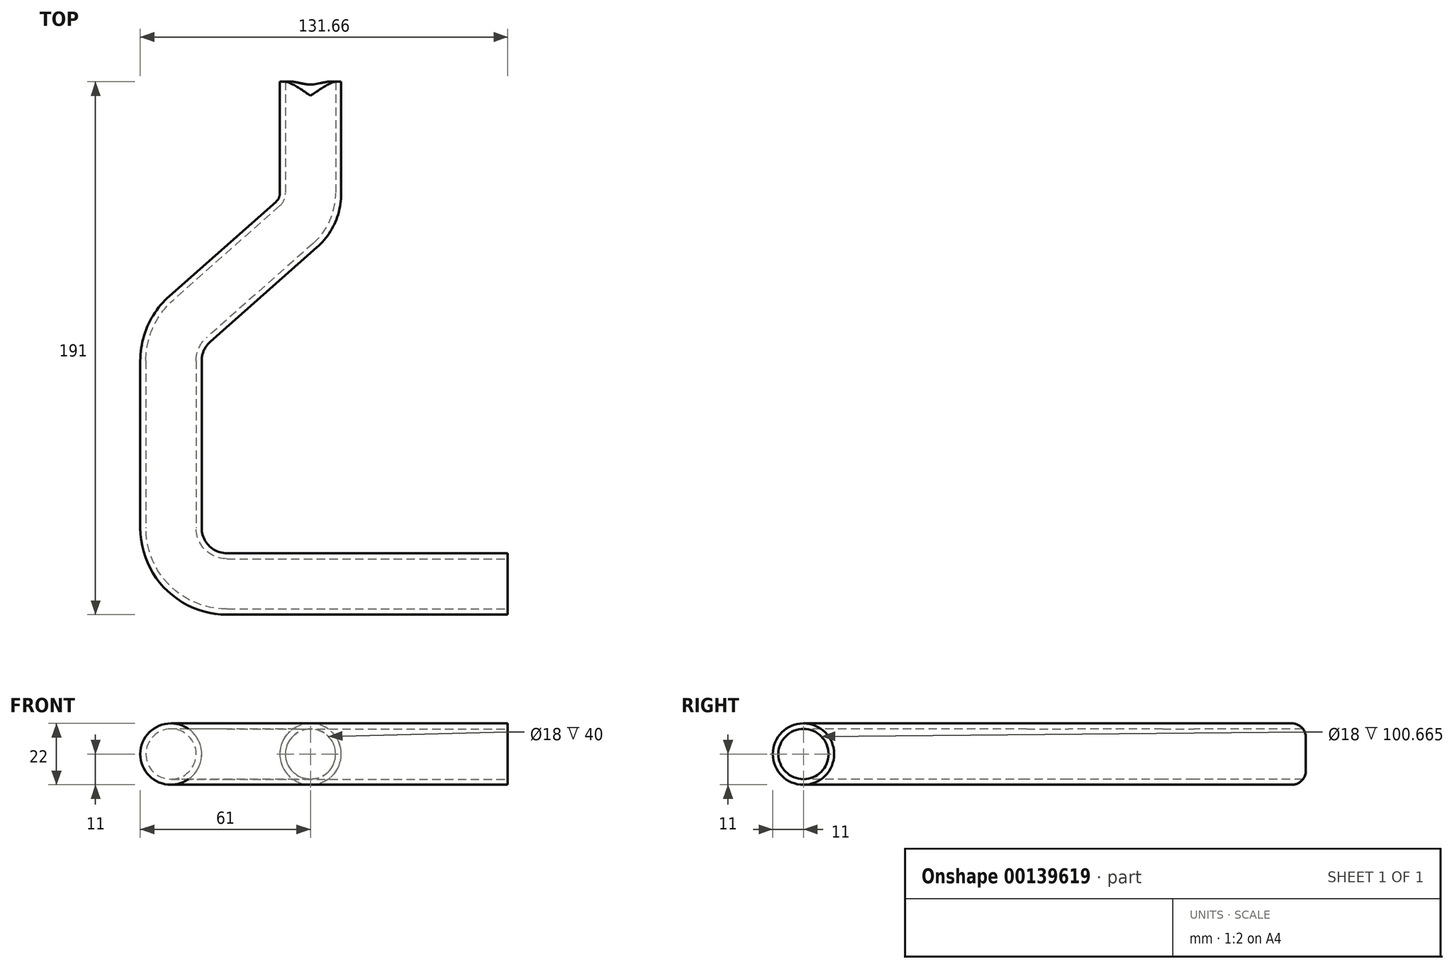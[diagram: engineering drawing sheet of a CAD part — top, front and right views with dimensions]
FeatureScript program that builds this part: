
annotation { "Feature Type Name" : "Feature", "Feature Type Description" : "" }
export const myFeature = defineFeature(function(context is Context, id is Id, definition is map)
    precondition{}
    {
        {
            var Q0;
            Q0=qCreatedBy(makeId("Front.planeOp"),FACE);
            var sketch = newSketch(context, id + "F0", { "sketchPlane" : qUnion([Q0])});
            skCircle(sketch, "E0", {"center": v(0, 0) * mm, "radius": 9 * mm});
            skCircle(sketch, "E1", {"center": v(0, 0) * mm, "radius": 11 * mm});
            skSolve(sketch);
        }
        {
            var Q0;
            Q0=qCreatedBy(makeId("Top.planeOp"),FACE);
            var sketch = newSketch(context, id + "F1", { "sketchPlane" : qUnion([Q0])});
            skLineSegment(sketch, "E2", {"start": v(0, 0) * mm, "end": v(0, -40) * mm});
            skLineSegment(sketch, "E3", {"start": v(-5.06, -51.23) * mm, "end": v(-43.25, -85.02) * mm});
            skLineSegment(sketch, "E4", {"start": v(-50, -100) * mm, "end": v(-50, -160) * mm});
            skLineSegment(sketch, "E5", {"start": v(-30, -180) * mm, "end": v(70.66, -180) * mm});
            skPoint(sketch, "E6.visualSharp", {"position": v(0, -46.76) * mm});
            skArc(sketch, "E6.filletArc", {"start": v(-5.06, -51.23) * mm, "mid": v(-1.32, -46.16) * mm, "end": v(0, -40) * mm});
            skPoint(sketch, "E7.visualSharp", {"position": v(-50, -91) * mm});
            skArc(sketch, "E7.filletArc", {"start": v(-43.25, -85.02) * mm, "mid": v(-48.24, -91.79) * mm, "end": v(-50, -100) * mm});
            skPoint(sketch, "E8.visualSharp", {"position": v(-50, -180) * mm});
            skArc(sketch, "E8.filletArc", {"start": v(-50, -160) * mm, "mid": v(-44.14, -174.14) * mm, "end": v(-30, -180) * mm});
            skSolve(sketch);
        }
        {
            var Q0;
            Q0 = qSketchRegion(id + "F0", true);
            var Q1;
            Q1 = qConstructionFilter(qBodyType(qCreatedBy(id + "F1" ,EDGE), BodyType.WIRE), ConstructionObject.NO);
            sweep(context, id + "F2", {"profiles" : qUnion([Q0]), "path" : qUnion([Q1])});
        }
        {
            var Q0;
            Q0=qCreatedBy(makeId("Right.planeOp"),FACE);
            var sketch = newSketch(context, id + "F3", { "sketchPlane" : qUnion([Q0])});
            skLineSegment(sketch, "E9", {"start": v(0, 0) * mm, "end": v(0, -6) * mm});
            skLineSegment(sketch, "E10", {"start": v(-5, -11) * mm, "end": v(-6.28, -11) * mm});
            skPoint(sketch, "E11.newPointB", {"position": v(0, -11.96) * mm});
            skArc(sketch, "E11.filletArc", {"start": v(-5, -11) * mm, "mid": v(-1.46, -9.54) * mm, "end": v(0, -6) * mm});
            skLineSegment(sketch, "E12", {"start": v(-6.28, -11) * mm, "end": v(-6.28, -17.01) * mm});
            skLineSegment(sketch, "E13", {"start": v(-6.28, -17.01) * mm, "end": v(9.81, -17.01) * mm});
            skLineSegment(sketch, "E14", {"start": v(9.81, -17.01) * mm, "end": v(9.81, 0) * mm});
            skLineSegment(sketch, "E15", {"start": v(9.81, 0) * mm, "end": v(0, 0) * mm});
            skLineSegment(sketch, "E16.MirrorCS", {"start": v(-5, 11) * mm, "end": v(-6.28, 11) * mm});
            skPoint(sketch, "E17.MirrorP", {"position": v(0, 11.96) * mm});
            skLineSegment(sketch, "E18.MirrorCS", {"start": v(0, 0) * mm, "end": v(0, 6) * mm});
            skLineSegment(sketch, "E19.MirrorCS", {"start": v(9.81, 17.01) * mm, "end": v(9.81, 0) * mm});
            skLineSegment(sketch, "E20.MirrorCS", {"start": v(-6.28, 11) * mm, "end": v(-6.28, 17.01) * mm});
            skLineSegment(sketch, "E21.MirrorCS", {"start": v(-6.28, 17.01) * mm, "end": v(9.81, 17.01) * mm});
            skArc(sketch, "E22.MirrorCS", {"start": v(-5, 11) * mm, "mid": v(-1.46, 9.54) * mm, "end": v(0, 6) * mm});
            skSolve(sketch);
        }
        {
            var Q0;
            Q0=makeQuery(id+"F3.imprint","IMPRINT",FACE,{"disambiguationData":[TD([[makeQuery(id+"F3.imprint","IMPRINT",EDGE,{"derivedFrom":sQuery(id+"F3.wireOp",EDGE,"E15")}),-1.0]])]});
            var Q1;
            Q1=makeQuery(id+"F3.imprint","IMPRINT",FACE,{"disambiguationData":[TD([[makeQuery(id+"F3.imprint","IMPRINT",EDGE,{"derivedFrom":sQuery(id+"F3.wireOp",EDGE,"E9")}),1.0]])]});
            extrude(context, id + "F4", {"entities" : qUnion([Q0, Q1]), "operationType" : NewBodyOperationType.REMOVE, "oppositeDirection" : true, "depth" : 50 * mm, "symmetric" : true});
        }
    });
